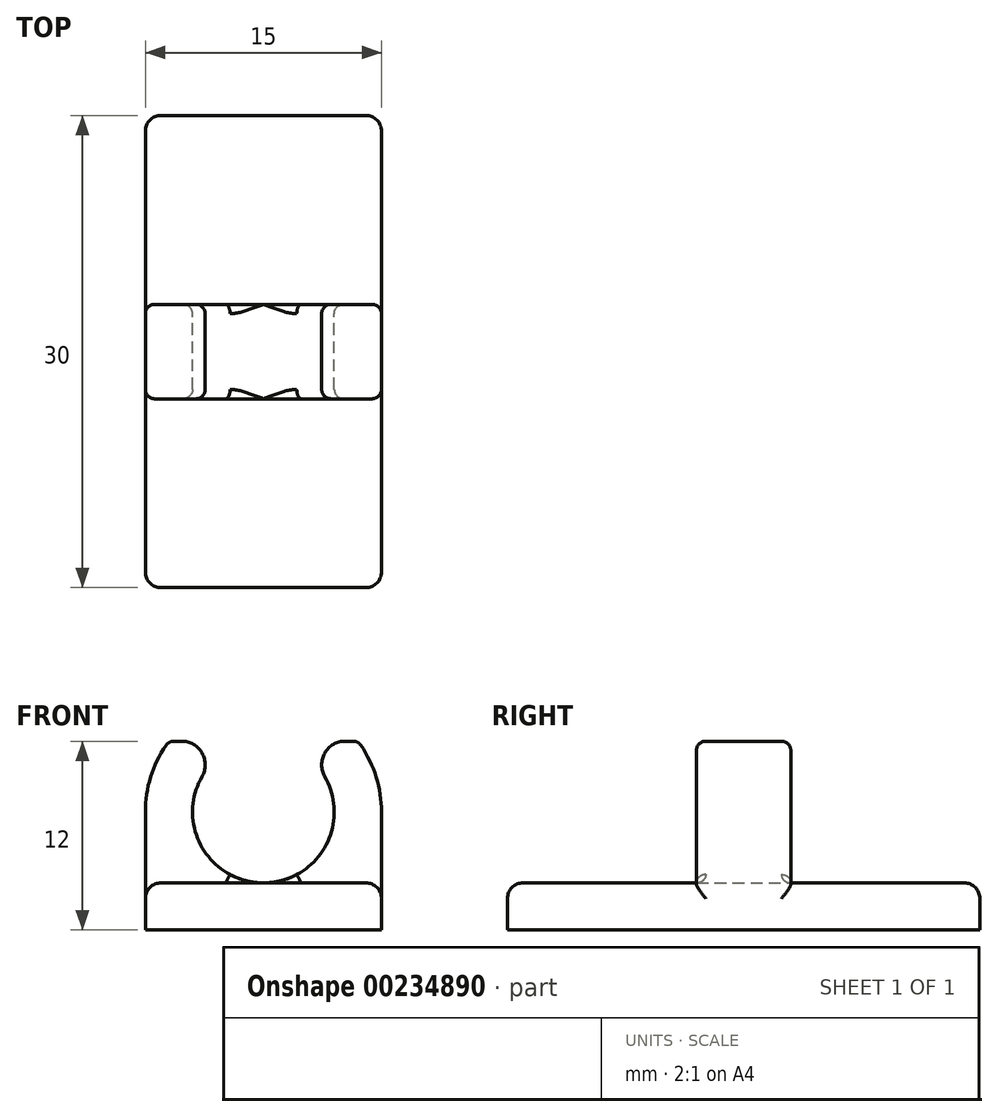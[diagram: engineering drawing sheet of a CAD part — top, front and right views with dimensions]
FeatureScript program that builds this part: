
annotation { "Feature Type Name" : "Feature", "Feature Type Description" : "" }
export const myFeature = defineFeature(function(context is Context, id is Id, definition is map)
    precondition{}
    {
        {
            var Q0;
            Q0=qCreatedBy(makeId("Front.planeOp"),FACE);
            var sketch = newSketch(context, id + "F0", { "sketchPlane" : qUnion([Q0])});
            skLineSegment(sketch, "E0.bottom", {"start": v(-7.5, 3) * mm, "end": v(7.5, 3) * mm});
            skLineSegment(sketch, "E0.top", {"start": v(-7.5, 0) * mm, "end": v(7.5, 0) * mm});
            skLineSegment(sketch, "E0.left", {"start": v(-7.5, 3) * mm, "end": v(-7.5, 0) * mm});
            skLineSegment(sketch, "E0.right", {"start": v(7.5, 3) * mm, "end": v(7.5, 0) * mm});
            skArc(sketch, "E1", {"start": v(-3.9, 9.75) * mm, "mid": v(0, 3) * mm, "end": v(3.9, 9.75) * mm});
            skArc(sketch, "E2.0", {"start": v(-6, 12) * mm, "mid": v(-7.12, 9.87) * mm, "end": v(-7.5, 7.5) * mm});
            skLineSegment(sketch, "E3", {"start": v(-6, 12) * mm, "end": v(-5.2, 12) * mm});
            skLineSegment(sketch, "E4.trimOffspring", {"start": v(5.2, 12) * mm, "end": v(6, 12) * mm});
            skPoint(sketch, "E5.visualSharp", {"position": v(0, 12) * mm});
            skArc(sketch, "E5.filletArc", {"start": v(5.2, 12) * mm, "mid": v(3.9, 11.25) * mm, "end": v(3.9, 9.75) * mm});
            skArc(sketch, "E6.filletArc", {"start": v(-3.9, 9.75) * mm, "mid": v(-3.9, 11.25) * mm, "end": v(-5.2, 12) * mm});
            skLineSegment(sketch, "E7", {"start": v(7.5, 0) * mm, "end": v(7.5, 7.5) * mm});
            skLineSegment(sketch, "E8", {"start": v(-7.5, 0) * mm, "end": v(-7.5, 7.5) * mm});
            skArc(sketch, "E9.trimOffspring", {"start": v(7.5, 7.5) * mm, "mid": v(7.12, 9.87) * mm, "end": v(6, 12) * mm});
            skSolve(sketch);
        }
        {
            var Q0;
            {var subQ0=sQuery(id+"F0.wireOp",EDGE,"E0.right");Q0=makeQuery(id+"F0.imprint","IMPRINT",FACE,{"disambiguationData":[TD([[makeQuery(id+"F0.imprint","IMPRINT",EDGE,{"derivedFrom":subQ0}),-1.0]])]});}
            var Q1;
            {var subQ0=sQuery(id+"F0.wireOp",EDGE,"E0.left");Q1=makeQuery(id+"F0.imprint","IMPRINT",FACE,{"disambiguationData":[TD([[makeQuery(id+"F0.imprint","IMPRINT",EDGE,{"derivedFrom":subQ0}),1.0]])]});}
            var Q2;
            {var subQ0=sQuery(id+"F0.wireOp",EDGE,"E2.0");var subQ1=sQuery(id+"F0.wireOp",EDGE,"E0.bottom");var subQ2=makeQuery(id+"F0.imprint","INTERSECT",VERTEX,{"disambiguationData":[OD(0.0)],"derivedFrom":[subQ1,subQ0]});Q2=makeQuery(id+"F0.imprint","IMPRINT",FACE,{"disambiguationData":[TD([[makeQuery(id+"F0.imprint","IMPRINT",EDGE,{"disambiguationData":[TD([[subQ2,-1.0]])],"derivedFrom":subQ1}),-1.0]])]});}
            extrude(context, id + "F1", {"entities" : qUnion([Q0, Q1, Q2]), "endBound" : BoundingType.SYMMETRIC, "depth" : 30 * mm});
        }
        {
            var Q0;
            {var subQ5=sQuery(id+"F0.wireOp",EDGE,"E3");Q0=makeQuery(id+"F0.imprint","IMPRINT",FACE,{"disambiguationData":[TD([[makeQuery(id+"F0.imprint","IMPRINT",EDGE,{"derivedFrom":subQ5}),-1.0]])]});}
            var Q1;
            {var subQ5=sQuery(id+"F0.wireOp",EDGE,"E4.trimOffspring");Q1=makeQuery(id+"F0.imprint","IMPRINT",FACE,{"disambiguationData":[TD([[makeQuery(id+"F0.imprint","IMPRINT",EDGE,{"derivedFrom":subQ5}),-1.0]])]});}
            extrude(context, id + "F2", {"entities" : qUnion([Q0, Q1]), "operationType" : NewBodyOperationType.ADD, "endBound" : BoundingType.SYMMETRIC, "depth" : 6 * mm});
        }
        {
            var Q0;
            Q0=makeQuery(id+"F2.opExtrude","SWEPT_EDGE",EDGE,{"disambiguationData":[OSD([sQuery(id+"F0.wireOp",EDGE,"E1"),sQuery(id+"F0.wireOp",EDGE,"E3")])]});
            var Q1;
            Q1=makeQuery(id+"F2.opExtrude","SWEPT_EDGE",EDGE,{"disambiguationData":[OSD([sQuery(id+"F0.wireOp",EDGE,"E1"),sQuery(id+"F0.wireOp",EDGE,"E4.trimOffspring")])]});
            var Q2;
            Q2=makeQuery(id+"F2.opExtrude","SWEPT_EDGE",EDGE,{"disambiguationData":[OSD([sQuery(id+"F0.wireOp",EDGE,"E2.0"),sQuery(id+"F0.wireOp",EDGE,"E3")])]});
            var Q3;
            Q3=makeQuery(id+"F2.opExtrude","SWEPT_EDGE",EDGE,{"disambiguationData":[OSD([sQuery(id+"F0.wireOp",EDGE,"E2.0"),sQuery(id+"F0.wireOp",EDGE,"E4.trimOffspring")])]});
            fillet(context, id + "F3", {"entities" : qUnion([Q0, Q1, Q2, Q3]), "radius" : 0.6 * mm, "tangentPropagation" : true, "allowEdgeOverflow" : false});
        }
        {
            var Q0;
            {var subQ0=sQuery(id+"F0.wireOp",EDGE,"E0.right");var subQ1=sQuery(id+"F0.wireOp",EDGE,"E0.bottom");var subQ2=sQuery(id+"F0.wireOp",EDGE,"E2.0");Q0=makeQuery(id+"F2.boolean.opBoolean","SPLIT",EDGE,{"disambiguationData":[TD([makeQuery(id+"F1.opExtrude","CAP_FACE",FACE,{"disambiguationData":[OSD([subQ1,sQuery(id+"F0.wireOp",EDGE,"E0.top"),sQuery(id+"F0.wireOp",EDGE,"E0.left"),subQ0])],"isStart":false})])],"derivedFrom":makeQuery(id+"F1.opExtrude","SWEPT_EDGE",EDGE,{"disambiguationData":[OSD([subQ1,subQ0,subQ2])]})});}
            var Q1;
            {var subQ1=sQuery(id+"F0.wireOp",EDGE,"E2.0");var subQ2=sQuery(id+"F0.wireOp",EDGE,"E0.bottom");var subQ3=sQuery(id+"F0.wireOp",EDGE,"E0.left");Q1=makeQuery(id+"F2.boolean.opBoolean","SPLIT",EDGE,{"disambiguationData":[TD([makeQuery(id+"F1.opExtrude","CAP_FACE",FACE,{"disambiguationData":[OSD([subQ2,sQuery(id+"F0.wireOp",EDGE,"E0.top"),subQ3,sQuery(id+"F0.wireOp",EDGE,"E0.right")])],"isStart":false})])],"derivedFrom":makeQuery(id+"F1.opExtrude","SWEPT_EDGE",EDGE,{"disambiguationData":[OSD([subQ2,subQ3,subQ1])]})});}
            var Q2;
            {var subQ0=sQuery(id+"F0.wireOp",EDGE,"E0.right");var subQ2=sQuery(id+"F0.wireOp",EDGE,"E2.0");var subQ3=sQuery(id+"F0.wireOp",EDGE,"E0.bottom");Q2=makeQuery(id+"F2.boolean.opBoolean","SPLIT",EDGE,{"disambiguationData":[TD([makeQuery(id+"F1.opExtrude","CAP_FACE",FACE,{"disambiguationData":[OSD([subQ3,sQuery(id+"F0.wireOp",EDGE,"E0.top"),sQuery(id+"F0.wireOp",EDGE,"E0.left"),subQ0])],"isStart":true})])],"derivedFrom":makeQuery(id+"F1.opExtrude","SWEPT_EDGE",EDGE,{"disambiguationData":[OSD([subQ3,subQ0,subQ2])]})});}
            var Q3;
            {var subQ1=sQuery(id+"F0.wireOp",EDGE,"E2.0");var subQ2=sQuery(id+"F0.wireOp",EDGE,"E0.bottom");var subQ3=sQuery(id+"F0.wireOp",EDGE,"E0.left");Q3=makeQuery(id+"F2.boolean.opBoolean","SPLIT",EDGE,{"disambiguationData":[TD([makeQuery(id+"F1.opExtrude","CAP_FACE",FACE,{"disambiguationData":[OSD([subQ2,sQuery(id+"F0.wireOp",EDGE,"E0.top"),subQ3,sQuery(id+"F0.wireOp",EDGE,"E0.right")])],"isStart":true})])],"derivedFrom":makeQuery(id+"F1.opExtrude","SWEPT_EDGE",EDGE,{"disambiguationData":[OSD([subQ2,subQ3,subQ1])]})});}
            fillet(context, id + "F4", {"entities" : qUnion([Q0, Q1, Q2, Q3]), "radius" : 1 * mm, "tangentPropagation" : true, "allowEdgeOverflow" : false});
        }
        {
            var Q0;
            Q0=makeQuery(id+"F1.opExtrude","CAP_EDGE",EDGE,{"disambiguationData":[OSD([sQuery(id+"F0.wireOp",EDGE,"E0.bottom")])],"isStart":true});
            var Q1;
            Q1=makeQuery(id+"F1.opExtrude","CAP_EDGE",EDGE,{"disambiguationData":[OSD([sQuery(id+"F0.wireOp",EDGE,"E0.bottom")])],"isStart":false});
            fillet(context, id + "F5", {"entities" : qUnion([Q0, Q1]), "radius" : 1 * mm, "tangentPropagation" : true, "allowEdgeOverflow" : false});
        }
        {
            var Q0;
            {var subQ0=sQuery(id+"F0.wireOp",EDGE,"E4.trimOffspring");var subQ1=sQuery(id+"F0.wireOp",EDGE,"E1");Q0=makeQuery(id+"F3.opFillet","BLEND_EDGE",EDGE,{"blendedFrom":[makeQuery(id+"F2.opExtrude","SWEPT_EDGE",EDGE,{"disambiguationData":[OSD([subQ1,subQ0])]}),makeQuery(id+"F2.opExtrude","CAP_FACE",FACE,{"disambiguationData":[OSD([sQuery(id+"F0.wireOp",EDGE,"E0.bottom"),subQ1,sQuery(id+"F0.wireOp",EDGE,"E2.0"),subQ0])],"isStart":true})],"blendedInto":[makeQuery(id+"F2.opExtrude","CAP_FACE",FACE,{"disambiguationData":[OSD([sQuery(id+"F0.wireOp",EDGE,"E0.bottom"),subQ1,sQuery(id+"F0.wireOp",EDGE,"E2.0"),subQ0])],"isStart":true})]});}
            var Q1;
            {var subQ0=sQuery(id+"F0.wireOp",EDGE,"E4.trimOffspring");var subQ1=sQuery(id+"F0.wireOp",EDGE,"E1");Q1=makeQuery(id+"F3.opFillet","BLEND_EDGE",EDGE,{"blendedFrom":[makeQuery(id+"F2.opExtrude","SWEPT_EDGE",EDGE,{"disambiguationData":[OSD([subQ1,subQ0])]}),makeQuery(id+"F2.opExtrude","CAP_FACE",FACE,{"disambiguationData":[OSD([sQuery(id+"F0.wireOp",EDGE,"E0.bottom"),subQ1,sQuery(id+"F0.wireOp",EDGE,"E2.0"),subQ0])],"isStart":false})],"blendedInto":[makeQuery(id+"F2.opExtrude","CAP_FACE",FACE,{"disambiguationData":[OSD([sQuery(id+"F0.wireOp",EDGE,"E0.bottom"),subQ1,sQuery(id+"F0.wireOp",EDGE,"E2.0"),subQ0])],"isStart":false})]});}
            fillet(context, id + "F6", {"entities" : qUnion([Q0, Q1]), "radius" : 0.6 * mm, "tangentPropagation" : true, "allowEdgeOverflow" : false});
        }
    });
